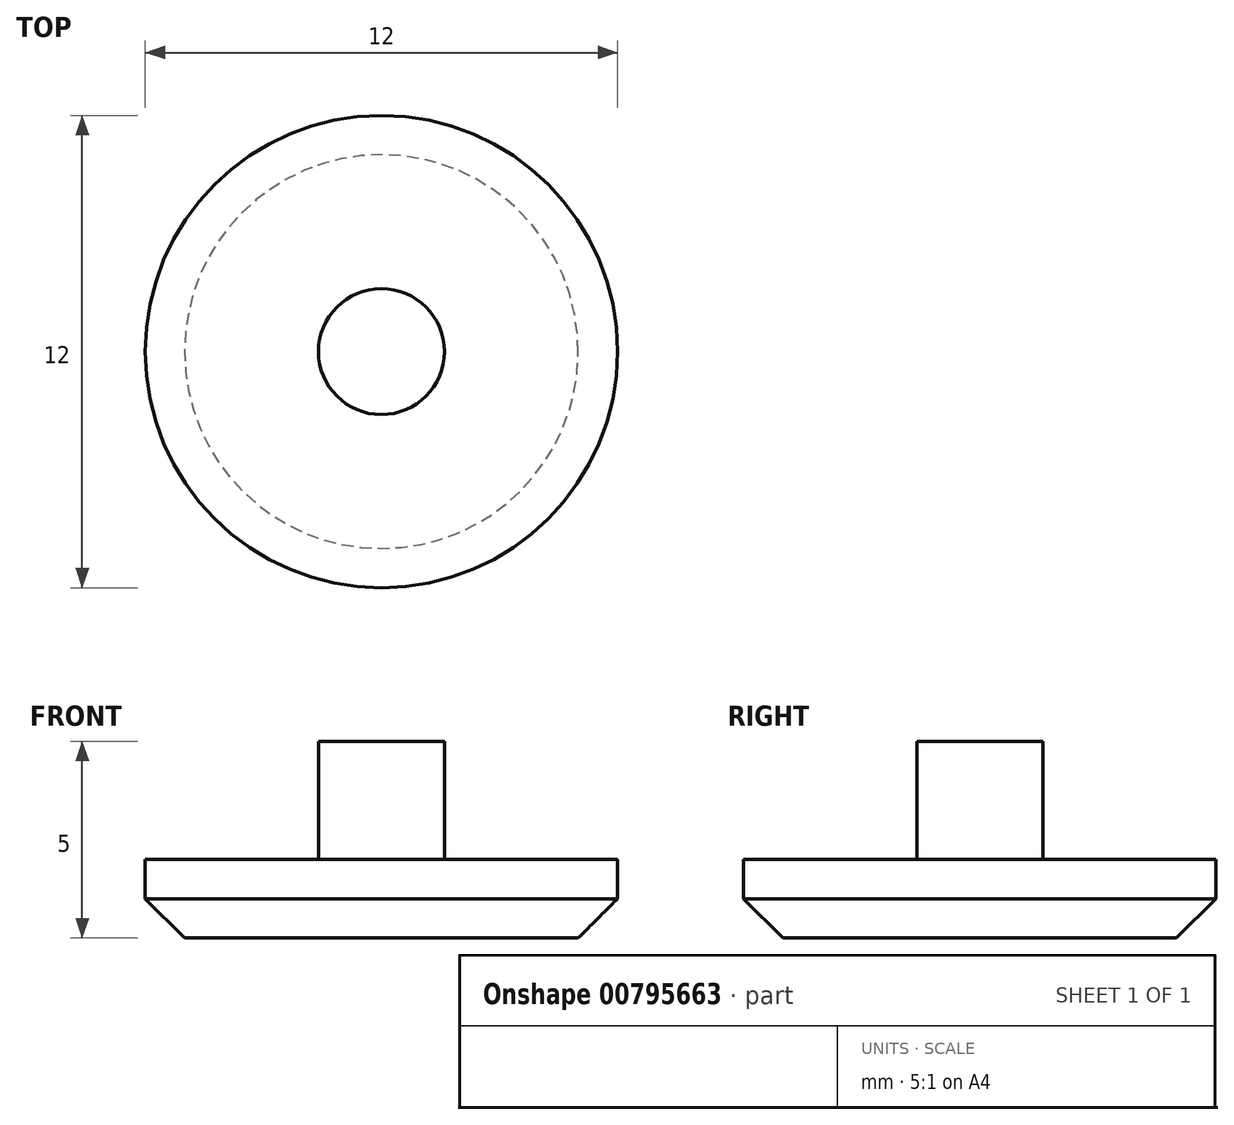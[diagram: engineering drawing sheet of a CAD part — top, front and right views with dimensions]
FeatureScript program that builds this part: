
annotation { "Feature Type Name" : "Feature", "Feature Type Description" : "" }
export const myFeature = defineFeature(function(context is Context, id is Id, definition is map)
    precondition{}
    {
        {
            var Q0;
            Q0=qCreatedBy(makeId("Top.planeOp"),FACE);
            var sketch = newSketch(context, id + "F0", { "sketchPlane" : qUnion([Q0])});
            skCircle(sketch, "E0", {"center": v(0, 0) * mm, "radius": 1.6 * mm});
            skCircle(sketch, "E1", {"center": v(0, 0) * mm, "radius": 6 * mm});
            skSolve(sketch);
        }
        {
            var Q0;
            Q0=makeQuery(id+"F0.imprint","IMPRINT",FACE,{"disambiguationData":[TD([[makeQuery(id+"F0.imprint","IMPRINT",EDGE,{"derivedFrom":sQuery(id+"F0.wireOp",EDGE,"E0")}),-1.0]])]});
            extrude(context, id + "F1", {"entities" : qUnion([Q0]), "depth" : 2 * mm, "offsetDistance" : 25 * mm});
        }
        {
            var Q0;
            Q0=makeQuery(id+"F0.imprint","IMPRINT",FACE,{"disambiguationData":[TD([[makeQuery(id+"F0.imprint","IMPRINT",EDGE,{"derivedFrom":sQuery(id+"F0.wireOp",EDGE,"E0")}),1.0]])]});
            extrude(context, id + "F2", {"entities" : qUnion([Q0]), "operationType" : NewBodyOperationType.ADD, "depth" : 5 * mm, "offsetDistance" : 25 * mm});
        }
        {
            var Q0;
            Q0=makeQuery(id+"F1.opExtrude","CAP_EDGE",EDGE,{"disambiguationData":[OSD([sQuery(id+"F0.wireOp",EDGE,"E1")])],"isStart":true});
            var Q1;
            Q1=makeQuery(id+"F1.opExtrude","CAP_EDGE",EDGE,{"disambiguationData":[OSD([sQuery(id+"F0.wireOp",EDGE,"E0")])],"isStart":false});
            chamfer(context, id + "F3", {"entities" : qUnion([Q0, Q1]), "width" : 1 * mm, "tangentPropagation" : true});
        }
    });
